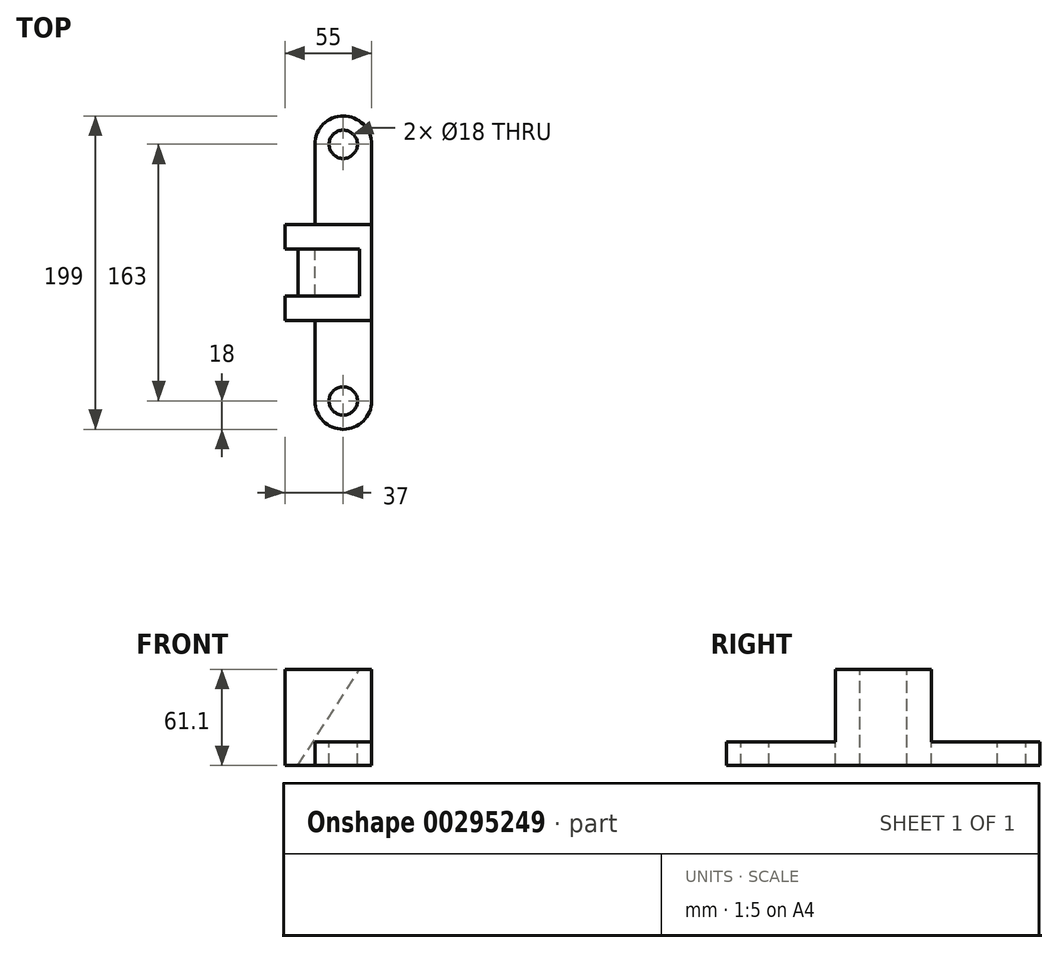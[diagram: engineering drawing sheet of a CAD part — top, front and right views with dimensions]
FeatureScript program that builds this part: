
annotation { "Feature Type Name" : "Feature", "Feature Type Description" : "" }
export const myFeature = defineFeature(function(context is Context, id is Id, definition is map)
    precondition{}
    {
        {
            var Q0;
            Q0=qCreatedBy(makeId("Right.planeOp"),FACE);
            var sketch = newSketch(context, id + "F0", { "sketchPlane" : qUnion([Q0])});
            skLineSegment(sketch, "E0.bottom", {"start": v(-30.5, 30.5) * mm, "end": v(30.5, 30.5) * mm});
            skLineSegment(sketch, "E0.top", {"start": v(-30.5, -30.5) * mm, "end": v(30.5, -30.5) * mm});
            skLineSegment(sketch, "E0.left", {"start": v(-30.5, 30.5) * mm, "end": v(-30.5, -30.5) * mm});
            skLineSegment(sketch, "E0.right", {"start": v(30.5, 30.5) * mm, "end": v(30.5, -30.5) * mm});
            skLineSegment(sketch, "E1", {"start": v(-30.5, -15.5) * mm, "end": v(-81.5, -15.5) * mm});
            skLineSegment(sketch, "E2", {"start": v(-81.5, -15.5) * mm, "end": v(-81.5, -30.5) * mm});
            skLineSegment(sketch, "E3", {"start": v(-81.5, -30.5) * mm, "end": v(-30.5, -30.5) * mm});
            skLineSegment(sketch, "E4", {"start": v(30.5, -15.5) * mm, "end": v(81.5, -15.5) * mm});
            skLineSegment(sketch, "E5", {"start": v(81.5, -15.5) * mm, "end": v(81.5, -30.5) * mm});
            skLineSegment(sketch, "E6", {"start": v(81.5, -30.5) * mm, "end": v(30.5, -30.5) * mm});
            skLineSegment(sketch, "E7", {"start": v(-81.5, -15.5) * mm, "end": v(-99.5, -15.5) * mm});
            skLineSegment(sketch, "E8", {"start": v(-99.5, -15.5) * mm, "end": v(-99.5, -30.6) * mm});
            skLineSegment(sketch, "E9", {"start": v(-99.5, -30.6) * mm, "end": v(-81.5, -30.5) * mm});
            skLineSegment(sketch, "E10", {"start": v(81.5, -15.5) * mm, "end": v(99.5, -15.5) * mm});
            skLineSegment(sketch, "E11", {"start": v(99.5, -15.5) * mm, "end": v(99.5, -30.6) * mm});
            skLineSegment(sketch, "E12", {"start": v(99.5, -30.6) * mm, "end": v(81.5, -30.5) * mm});
            skSolve(sketch);
        }
        {
            var Q0;
            Q0 = qSketchRegion(id + "F0", true);
            extrude(context, id + "F1", {"entities" : qUnion([Q0]), "depth" : 36 * mm});
        }
        {
            var Q0;
            Q0=makeQuery(id+"F1.opExtrude","SWEPT_FACE",FACE,{"disambiguationData":[OSD([sQuery(id+"F0.wireOp",EDGE,"E0.bottom")])]});
            var sketch = newSketch(context, id + "F2", { "sketchPlane" : qUnion([Q0])});
            skLineSegment(sketch, "E13", {"start": v(36, -30.5) * mm, "end": v(36, 30.5) * mm});
            skLineSegment(sketch, "E14", {"start": v(36, 30.5) * mm, "end": v(-19, 30.5) * mm});
            skLineSegment(sketch, "E15", {"start": v(-19, 30.5) * mm, "end": v(-19, 15) * mm});
            skLineSegment(sketch, "E16", {"start": v(-19, 15) * mm, "end": v(28, 15) * mm});
            skLineSegment(sketch, "E17", {"start": v(28, 15) * mm, "end": v(28, -15) * mm});
            skLineSegment(sketch, "E18", {"start": v(28, -15) * mm, "end": v(-19, -15) * mm});
            skLineSegment(sketch, "E19", {"start": v(-19, -15) * mm, "end": v(-19, -30.5) * mm});
            skLineSegment(sketch, "E20", {"start": v(-19, -30.5) * mm, "end": v(0, -30.5) * mm});
            skPoint(sketch, "E21.center.orphan", {"position": v(18, 81.5) * mm});
            skPoint(sketch, "E22.center.orphan", {"position": v(18, -81.5) * mm});
            skLineSegment(sketch, "E23", {"start": v(-19, 15) * mm, "end": v(-19, -15) * mm});
            skCircle(sketch, "E24", {"center": v(18, 81.5) * mm, "radius": 18 * mm});
            skCircle(sketch, "E25", {"center": v(18, -81.5) * mm, "radius": 18 * mm});
            skLineSegment(sketch, "E26", {"start": v(36, 99.5) * mm, "end": v(36, -99.5) * mm});
            skLineSegment(sketch, "E27", {"start": v(36, -99.5) * mm, "end": v(0, -99.5) * mm});
            skLineSegment(sketch, "E28", {"start": v(0, -99.5) * mm, "end": v(0, 99.5) * mm});
            skLineSegment(sketch, "E29", {"start": v(0, 99.5) * mm, "end": v(36, 99.5) * mm});
            skCircle(sketch, "E30", {"center": v(18, 81.5) * mm, "radius": 9 * mm});
            skCircle(sketch, "E31", {"center": v(18, -81.5) * mm, "radius": 9 * mm});
            skLineSegment(sketch, "E32", {"start": v(36, -30.5) * mm, "end": v(0, -30.5) * mm});
            skSolve(sketch);
        }
        {
            var Q0;
            Q0=qCreatedBy(makeId("Top.planeOp"),FACE);
            var sketch = newSketch(context, id + "F3", { "sketchPlane" : qUnion([Q0])});
            skCircle(sketch, "E33", {"center": v(18, 81.5) * mm, "radius": 9 * mm});
            skCircle(sketch, "E34", {"center": v(18, -81.5) * mm, "radius": 9 * mm});
            skSolve(sketch);
        }
        {
            var Q0;
            Q0 = qSketchRegion(id + "F3", true);
            extrude(context, id + "F4", {"entities" : qUnion([Q0]), "operationType" : NewBodyOperationType.REMOVE, "oppositeDirection" : true, "depth" : 103.1 * mm});
        }
        {
            var Q0;
            Q0=qCreatedBy(makeId("Front.planeOp"),FACE);
            var sketch = newSketch(context, id + "F5", { "sketchPlane" : qUnion([Q0])});
            skLineSegment(sketch, "E35", {"start": v(36.36, 30.74) * mm, "end": v(-18.64, 30.74) * mm});
            skLineSegment(sketch, "E36", {"start": v(-18.64, 30.74) * mm, "end": v(-18.64, -30.26) * mm});
            skLineSegment(sketch, "E37", {"start": v(-18.64, -30.26) * mm, "end": v(36.36, -30.26) * mm});
            skLineSegment(sketch, "E38", {"start": v(36.36, -30.26) * mm, "end": v(36.36, 30.74) * mm});
            skLineSegment(sketch, "E39", {"start": v(-10.64, -30.26) * mm, "end": v(28.61, 30.74) * mm});
            skLineSegment(sketch, "E40", {"start": v(0, -30.26) * mm, "end": v(0, -13.73) * mm});
            skSolve(sketch);
        }
        {
            var Q0;
            {var subQ0=sQuery(id+"F5.wireOp",EDGE,"E36");Q0=makeQuery(id+"F5.imprint","IMPRINT",FACE,{"disambiguationData":[TD([[makeQuery(id+"F5.imprint","IMPRINT",EDGE,{"derivedFrom":subQ0}),1.0]])]});}
            extrude(context, id + "F6", {"entities" : qUnion([Q0]), "operationType" : NewBodyOperationType.REMOVE, "depth" : 15 * mm});
        }
        {
            var Q0;
            {var subQ0=sQuery(id+"F5.wireOp",EDGE,"E36");Q0=makeQuery(id+"F5.imprint","IMPRINT",FACE,{"disambiguationData":[TD([[makeQuery(id+"F5.imprint","IMPRINT",EDGE,{"derivedFrom":subQ0}),1.0]])]});}
            extrude(context, id + "F7", {"entities" : qUnion([Q0]), "operationType" : NewBodyOperationType.REMOVE, "oppositeDirection" : true, "depth" : 15 * mm});
        }
        {
            var Q0;
            {var subQ3=sQuery(id+"F2.wireOp",EDGE,"E15");Q0=makeQuery(id+"F2.imprint","IMPRINT",FACE,{"disambiguationData":[TD([[makeQuery(id+"F2.imprint","IMPRINT",EDGE,{"derivedFrom":subQ3}),1.0]])]});}
            var Q1;
            {var subQ0=sQuery(id+"F2.wireOp",EDGE,"E19");Q1=makeQuery(id+"F2.imprint","IMPRINT",FACE,{"disambiguationData":[TD([[makeQuery(id+"F2.imprint","IMPRINT",EDGE,{"derivedFrom":subQ0}),1.0]])]});}
            extrude(context, id + "F8", {"entities" : qUnion([Q0, Q1]), "operationType" : NewBodyOperationType.ADD, "oppositeDirection" : true, "depth" : 61 * mm});
        }
        {
            var Q0;
            {var subQ0=sQuery(id+"F2.wireOp",EDGE,"E29");var subQ1=sQuery(id+"F2.wireOp",EDGE,"E24");var subQ2=makeQuery(id+"F2.imprint","INTERSECT",VERTEX,{"disambiguationData":[OD(0.0)],"derivedFrom":[subQ1,subQ0]});Q0=makeQuery(id+"F2.imprint","IMPRINT",FACE,{"disambiguationData":[TD([[makeQuery(id+"F2.imprint","IMPRINT",EDGE,{"disambiguationData":[TD([[subQ2,1.0]])],"derivedFrom":subQ1}),-1.0]])]});}
            var Q1;
            {var subQ0=sQuery(id+"F2.wireOp",EDGE,"E29");var subQ1=sQuery(id+"F2.wireOp",EDGE,"E24");var subQ2=makeQuery(id+"F2.imprint","INTERSECT",VERTEX,{"disambiguationData":[OD(1.0)],"derivedFrom":[subQ1,subQ0]});Q1=makeQuery(id+"F2.imprint","IMPRINT",FACE,{"disambiguationData":[TD([[makeQuery(id+"F2.imprint","IMPRINT",EDGE,{"disambiguationData":[TD([[subQ2,-1.0]])],"derivedFrom":subQ1}),-1.0]])]});}
            extrude(context, id + "F9", {"entities" : qUnion([Q0, Q1]), "operationType" : NewBodyOperationType.REMOVE, "oppositeDirection" : true, "depth" : 100 * mm});
        }
        {
            var Q0;
            {var subQ0=sQuery(id+"F2.wireOp",EDGE,"E28");var subQ1=sQuery(id+"F2.wireOp",EDGE,"E25");var subQ2=makeQuery(id+"F2.imprint","INTERSECT",VERTEX,{"derivedFrom":[subQ1,subQ0]});Q0=makeQuery(id+"F2.imprint","IMPRINT",FACE,{"disambiguationData":[TD([[makeQuery(id+"F2.imprint","IMPRINT",EDGE,{"disambiguationData":[TD([[subQ2,-1.0]])],"derivedFrom":subQ1}),-1.0]])]});}
            var Q1;
            {var subQ0=sQuery(id+"F2.wireOp",EDGE,"E26");var subQ1=sQuery(id+"F2.wireOp",EDGE,"E25");var subQ2=makeQuery(id+"F2.imprint","INTERSECT",VERTEX,{"derivedFrom":[subQ1,subQ0]});Q1=makeQuery(id+"F2.imprint","IMPRINT",FACE,{"disambiguationData":[TD([[makeQuery(id+"F2.imprint","IMPRINT",EDGE,{"disambiguationData":[TD([[subQ2,1.0]])],"derivedFrom":subQ1}),-1.0]])]});}
            extrude(context, id + "F10", {"entities" : qUnion([Q0, Q1]), "operationType" : NewBodyOperationType.REMOVE, "oppositeDirection" : true, "depth" : 100 * mm});
        }
        {
            var Q0;
            {var subQ3=sQuery(id+"F5.wireOp",EDGE,"E40");Q0=makeQuery(id+"F5.imprint","IMPRINT",FACE,{"disambiguationData":[TD([[makeQuery(id+"F5.imprint","IMPRINT",EDGE,{"derivedFrom":subQ3}),1.0]])]});}
            extrude(context, id + "F11", {"entities" : qUnion([Q0]), "operationType" : NewBodyOperationType.ADD, "depth" : 25 * mm});
        }
        {
            var Q0;
            {var subQ3=sQuery(id+"F5.wireOp",EDGE,"E40");Q0=makeQuery(id+"F5.imprint","IMPRINT",FACE,{"disambiguationData":[TD([[makeQuery(id+"F5.imprint","IMPRINT",EDGE,{"derivedFrom":subQ3}),1.0]])]});}
            extrude(context, id + "F12", {"entities" : qUnion([Q0]), "operationType" : NewBodyOperationType.ADD, "oppositeDirection" : true, "depth" : 25 * mm});
        }
    });
